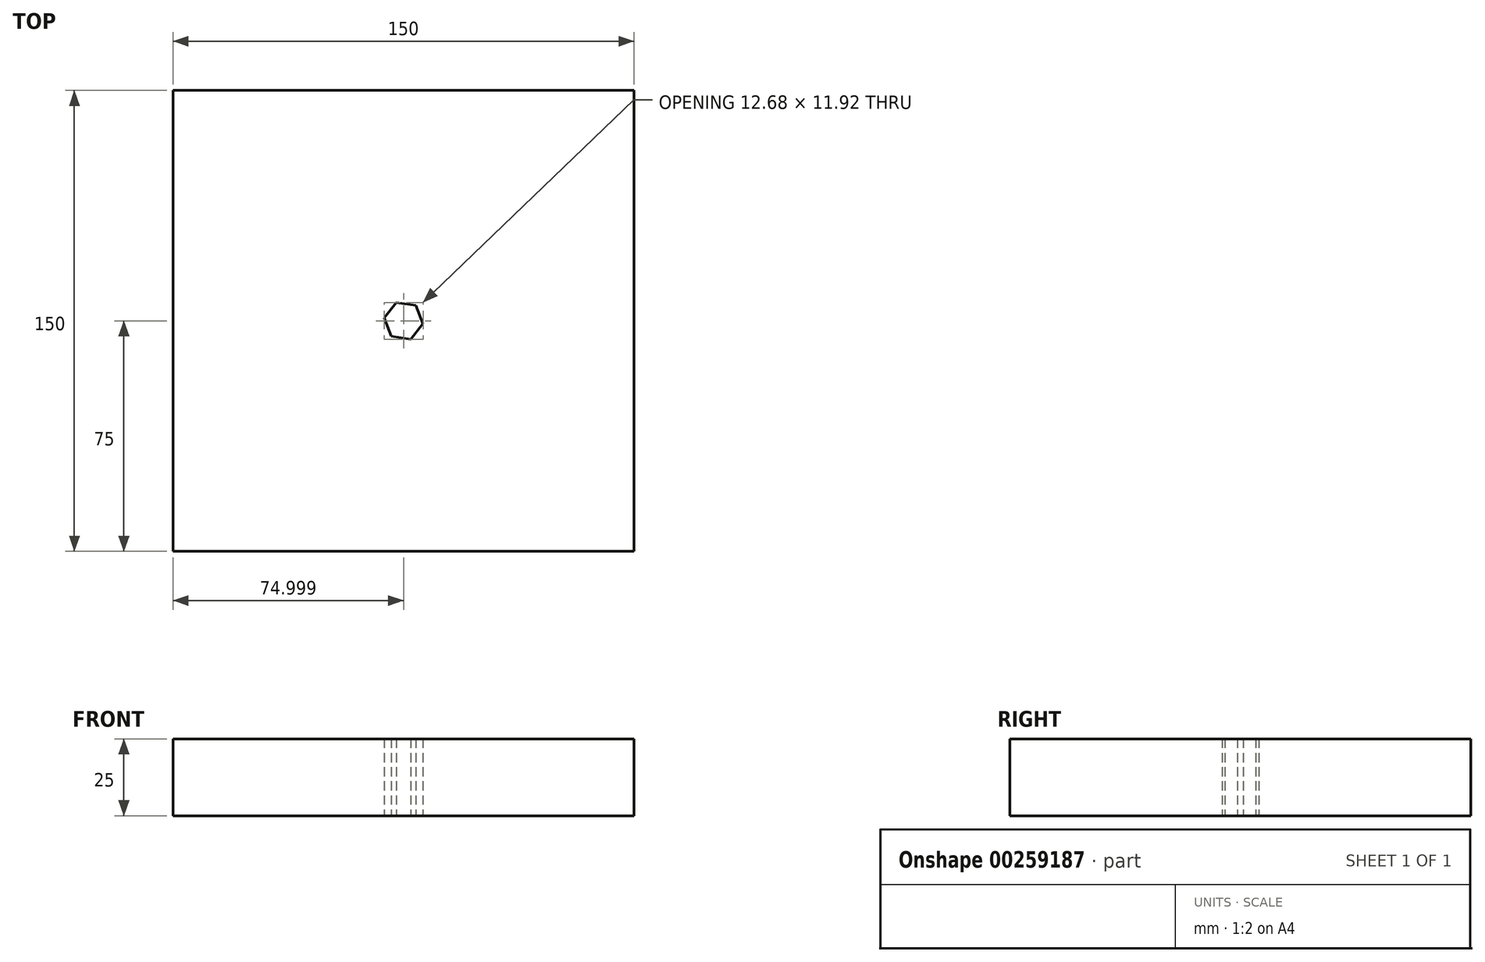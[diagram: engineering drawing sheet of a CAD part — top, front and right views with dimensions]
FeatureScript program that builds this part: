
annotation { "Feature Type Name" : "Feature", "Feature Type Description" : "" }
export const myFeature = defineFeature(function(context is Context, id is Id, definition is map)
    precondition{}
    {
        {
            var Q0;
            Q0=qCreatedBy(makeId("Top.planeOp"),FACE);
            var sketch = newSketch(context, id + "F0", { "sketchPlane" : qUnion([Q0])});
            skLineSegment(sketch, "E0.bottom", {"start": v(-226.24, -71.3) * mm, "end": v(-76.24, -71.3) * mm});
            skLineSegment(sketch, "E0.top", {"start": v(-226.24, 78.7) * mm, "end": v(-76.24, 78.7) * mm});
            skLineSegment(sketch, "E0.left", {"start": v(-226.24, -71.3) * mm, "end": v(-226.24, 78.7) * mm});
            skLineSegment(sketch, "E0.right", {"start": v(-76.24, -71.3) * mm, "end": v(-76.24, 78.7) * mm});
            skCircle(sketch, "E1.cCircle", {"center": v(-151.24, 3.7) * mm, "radius": 5.55 * mm, "construction": true});
            skPoint(sketch, "E1.cCircle.centerSnap0", {"position": v(-116.9, 3.7) * mm});
            skPoint(sketch, "E1.cCircle.centerSnap1", {"position": v(-151.24, -3.94) * mm});
            skLineSegment(sketch, "E1.0", {"start": v(-147.25, 8.73) * mm, "end": v(-144.9, 2.76) * mm});
            skLineSegment(sketch, "E1.1", {"start": v(-144.9, 2.76) * mm, "end": v(-148.9, -2.25) * mm});
            skLineSegment(sketch, "E1.2", {"start": v(-148.9, -2.25) * mm, "end": v(-155.23, -1.3) * mm});
            skLineSegment(sketch, "E1.3", {"start": v(-155.23, -1.3) * mm, "end": v(-157.58, 4.66) * mm});
            skLineSegment(sketch, "E1.4", {"start": v(-157.58, 4.66) * mm, "end": v(-153.6, 9.67) * mm});
            skLineSegment(sketch, "E1.5", {"start": v(-153.6, 9.67) * mm, "end": v(-147.25, 8.73) * mm});
            skPoint(sketch, "E1.0.midPoint", {"position": v(-146.08, 5.74) * mm});
            skPoint(sketch, "E2", {"position": v(-152.61, 4.66) * mm});
            skPoint(sketch, "E3", {"position": v(-76.24, 3.7) * mm});
            skPoint(sketch, "E4", {"position": v(-151.24, -71.3) * mm});
            skSolve(sketch);
        }
        {
            var Q0;
            Q0=makeQuery(id+"F0.imprint","IMPRINT",FACE,{"disambiguationData":[TD([[makeQuery(id+"F0.imprint","IMPRINT",EDGE,{"derivedFrom":sQuery(id+"F0.wireOp",EDGE,"E0.bottom")}),1.0]])]});
            extrude(context, id + "F1", {"entities" : qUnion([Q0]), "depth" : 25 * mm, "offsetDistance" : 25 * mm});
        }
    });
